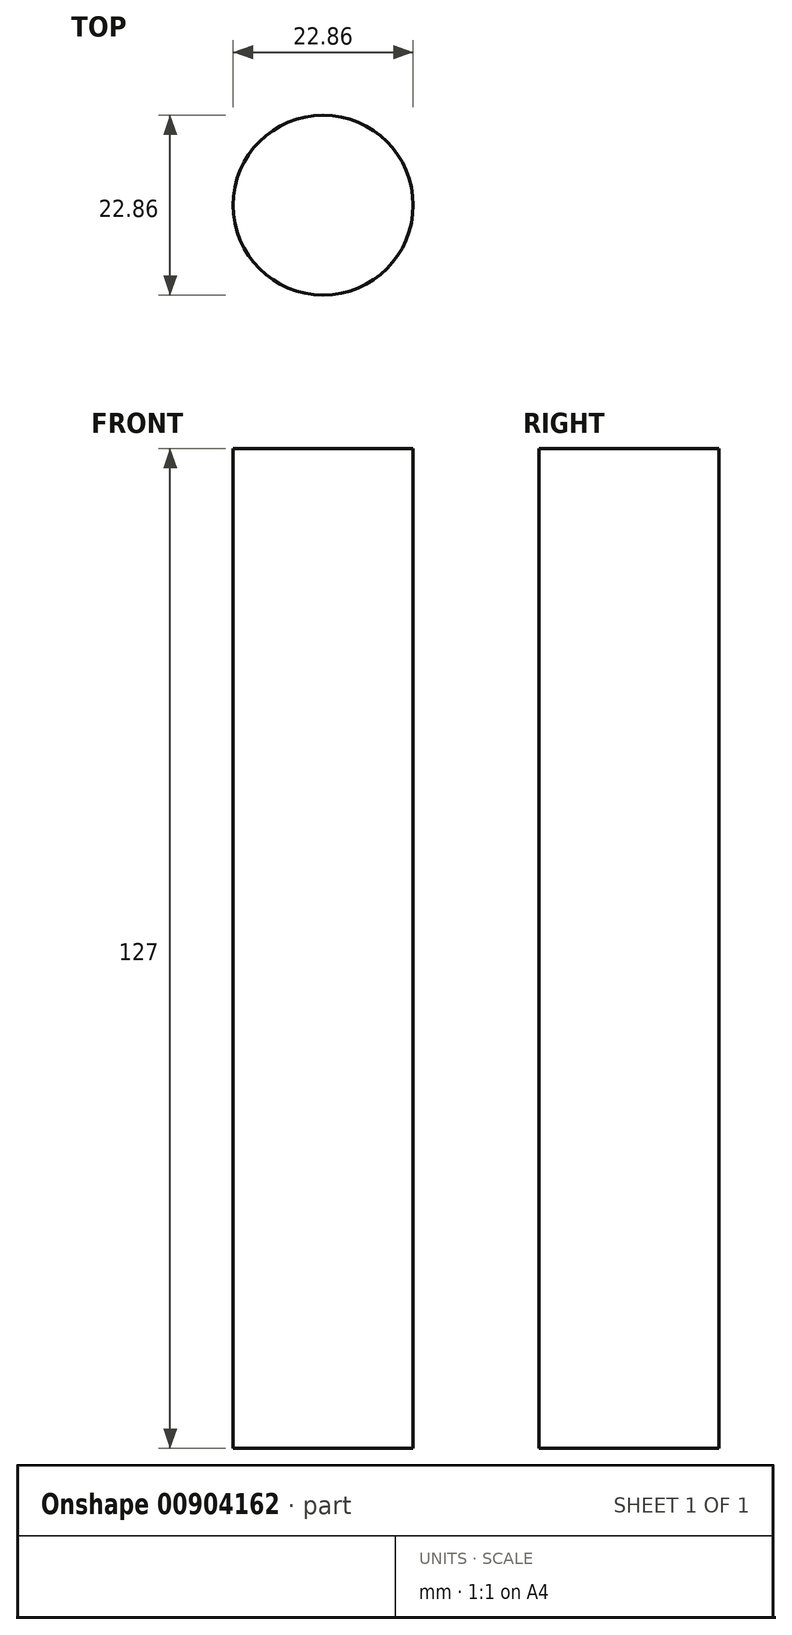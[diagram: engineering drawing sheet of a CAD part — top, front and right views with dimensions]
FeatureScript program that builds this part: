
annotation { "Feature Type Name" : "Feature", "Feature Type Description" : "" }
export const myFeature = defineFeature(function(context is Context, id is Id, definition is map)
    precondition{}
    {
        {
            var Q0;
            Q0=qCreatedBy(makeId("Top.planeOp"),FACE);
            var sketch = newSketch(context, id + "F0", { "sketchPlane" : qUnion([Q0])});
            skCircle(sketch, "E0", {"center": v(0, 0) * mm, "radius": 11.43 * mm});
            skSolve(sketch);
        }
        {
            var Q0;
            Q0=makeQuery(id+"F0.imprint","IMPRINT",FACE,{"disambiguationData":[TD([[makeQuery(id+"F0.imprint","IMPRINT",EDGE,{"derivedFrom":sQuery(id+"F0.wireOp",EDGE,"E0")}),1.0]])]});
            extrude(context, id + "F1", {"entities" : qUnion([Q0]), "depth" : 127 * mm, "offsetDistance" : 25.4 * mm});
        }
    });
